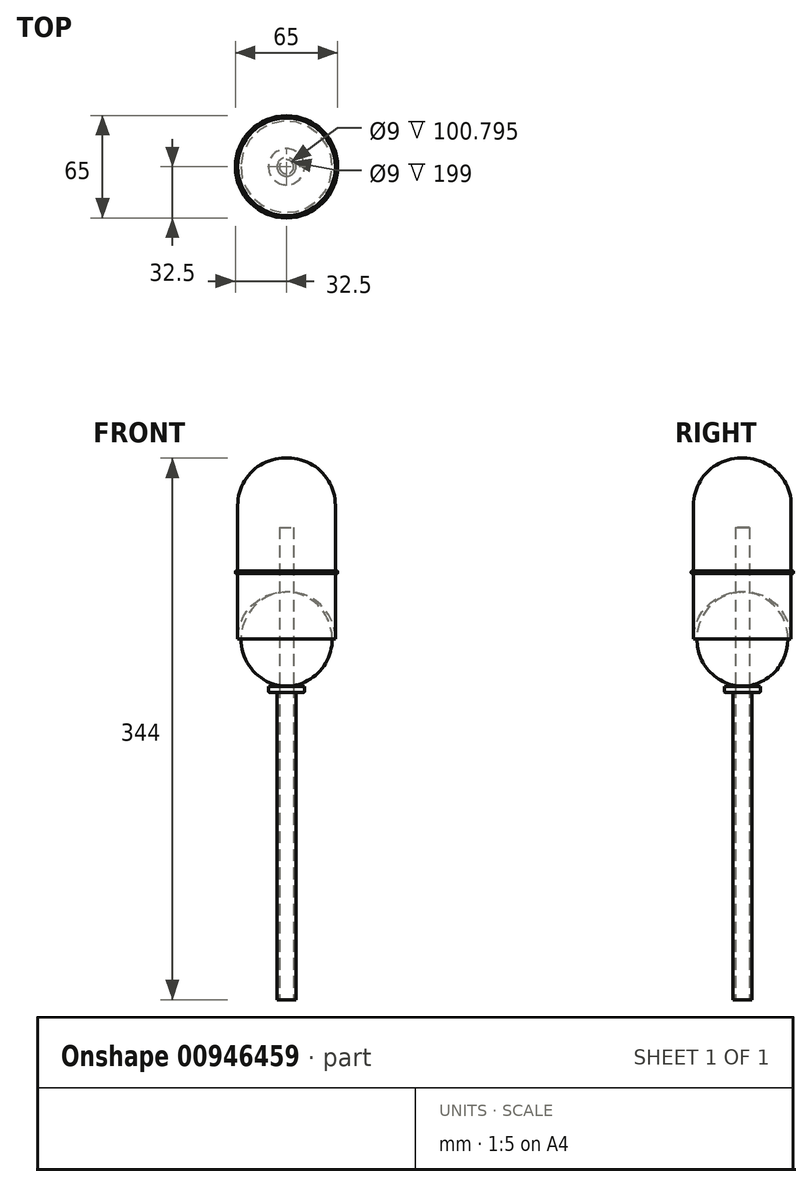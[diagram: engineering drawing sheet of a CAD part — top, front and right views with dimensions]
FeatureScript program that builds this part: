
annotation { "Feature Type Name" : "Feature", "Feature Type Description" : "" }
export const myFeature = defineFeature(function(context is Context, id is Id, definition is map)
    precondition{}
    {
        {
            var Q0;
            Q0=qCreatedBy(makeId("Top.planeOp"),FACE);
            var sketch = newSketch(context, id + "F0", { "sketchPlane" : qUnion([Q0])});
            skCircle(sketch, "E0", {"center": v(0, 0) * mm, "radius": 31 * mm});
            skSolve(sketch);
        }
        {
            var Q0;
            Q0 = qSketchRegion(id + "F0", true);
            extrude(context, id + "F1", {"entities" : qUnion([Q0]), "oppositeDirection" : true, "depth" : 145 * mm, "offsetDistance" : 25 * mm});
        }
        {
            var Q0;
            Q0=makeQuery(id+"F1.opExtrude","CAP_EDGE",EDGE,{"disambiguationData":[OSD([sQuery(id+"F0.wireOp",EDGE,"E0")])],"isStart":true});
            fillet(context, id + "F2", {"entities" : qUnion([Q0]), "radius" : 30 * mm, "tangentPropagation" : true, "allowEdgeOverflow" : false});
        }
        {
            var Q0;
            Q0=makeQuery(id+"F1.opExtrude","CAP_EDGE",EDGE,{"disambiguationData":[OSD([sQuery(id+"F0.wireOp",EDGE,"E0")])],"isStart":false});
            fillet(context, id + "F3", {"entities" : qUnion([Q0]), "radius" : 30 * mm, "tangentPropagation" : true, "allowEdgeOverflow" : false});
        }
        {
            var Q0;
            Q0=qCreatedBy(makeId("Top.planeOp"),FACE);
            cPlane(context, id + "F4", {"entities" : qUnion([Q0]), "cplaneType" : CPlaneType.OFFSET, "offset" : 72.5 * mm, "oppositeDirection" : true, "width" : 150 * mm, "height" : 150 * mm});
        }
        {
            var Q0;
            Q0=qCreatedBy(id+"F4.planeOp",FACE);
            var sketch = newSketch(context, id + "F5", { "sketchPlane" : qUnion([Q0])});
            skCircle(sketch, "E1", {"center": v(0, 0) * mm, "radius": 32.5 * mm});
            skSolve(sketch);
        }
        {
            var Q0;
            Q0 = qSketchRegion(id + "F5", true);
            extrude(context, id + "F6", {"entities" : qUnion([Q0]), "operationType" : NewBodyOperationType.ADD, "endBound" : BoundingType.SYMMETRIC, "depth" : 1.5 * mm, "offsetDistance" : 25 * mm});
        }
        {
            var Q0;
            Q0=makeQuery(id+"F6.opExtrude","CAP_EDGE",EDGE,{"disambiguationData":[OSD([sQuery(id+"F5.wireOp",EDGE,"E1")])],"isStart":false});
            var Q1;
            Q1=makeQuery(id+"F6.opExtrude","CAP_EDGE",EDGE,{"disambiguationData":[OSD([sQuery(id+"F5.wireOp",EDGE,"E1")])],"isStart":true});
            fillet(context, id + "F7", {"entities" : qUnion([Q0, Q1]), "radius" : 0.5 * mm, "tangentPropagation" : true, "allowEdgeOverflow" : false});
        }
        {
            var Q0;
            Q0=qCreatedBy(id+"F4.planeOp",FACE);
            cPlane(context, id + "F8", {"entities" : qUnion([Q0]), "cplaneType" : CPlaneType.OFFSET, "offset" : 72.5 * mm, "oppositeDirection" : true, "width" : 150 * mm, "height" : 150 * mm});
        }
        {
            var Q0;
            Q0=qCreatedBy(id+"F8.planeOp",FACE);
            var sketch = newSketch(context, id + "F9", { "sketchPlane" : qUnion([Q0])});
            skCircle(sketch, "E2", {"center": v(0, 0) * mm, "radius": 11.5 * mm});
            skSolve(sketch);
        }
        {
            var Q0;
            Q0 = qSketchRegion(id + "F9", true);
            extrude(context, id + "F10", {"entities" : qUnion([Q0]), "operationType" : NewBodyOperationType.ADD, "oppositeDirection" : true, "depth" : 4 * mm, "offsetDistance" : 25 * mm});
        }
        {
            var Q0;
            Q0=makeQuery(id+"F10.opExtrude","CAP_EDGE",EDGE,{"disambiguationData":[OSD([sQuery(id+"F9.wireOp",EDGE,"E2")])],"isStart":false});
            fillet(context, id + "F11", {"entities" : qUnion([Q0]), "radius" : 1 * mm, "tangentPropagation" : true, "allowEdgeOverflow" : false});
        }
        {
            var Q0;
            Q0=makeQuery(id+"F10.opExtrude","CAP_FACE",FACE,{"disambiguationData":[OSD([sQuery(id+"F9.wireOp",EDGE,"E2")])],"isStart":false});
            var sketch = newSketch(context, id + "F12", { "sketchPlane" : qUnion([Q0])});
            skCircle(sketch, "E3", {"center": v(0, 0) * mm, "radius": 6 * mm});
            skSolve(sketch);
        }
        {
            var Q0;
            Q0 = qSketchRegion(id + "F12", true);
            extrude(context, id + "F13", {"entities" : qUnion([Q0]), "operationType" : NewBodyOperationType.ADD, "depth" : 195 * mm, "offsetDistance" : 25 * mm});
        }
        {
            var Q0;
            Q0=makeQuery(id+"F13.opExtrude","CAP_FACE",FACE,{"disambiguationData":[OSD([sQuery(id+"F12.wireOp",EDGE,"E3")])],"isStart":false});
            var sketch = newSketch(context, id + "F14", { "sketchPlane" : qUnion([Q0])});
            skCircle(sketch, "E4", {"center": v(0, 0) * mm, "radius": 4.5 * mm});
            skSolve(sketch);
        }
        {
            var Q0;
            Q0 = qSketchRegion(id + "F14", true);
            extrude(context, id + "F15", {"entities" : qUnion([Q0]), "operationType" : NewBodyOperationType.REMOVE, "oppositeDirection" : true, "depth" : 300 * mm, "offsetDistance" : 25 * mm});
        }
    });
